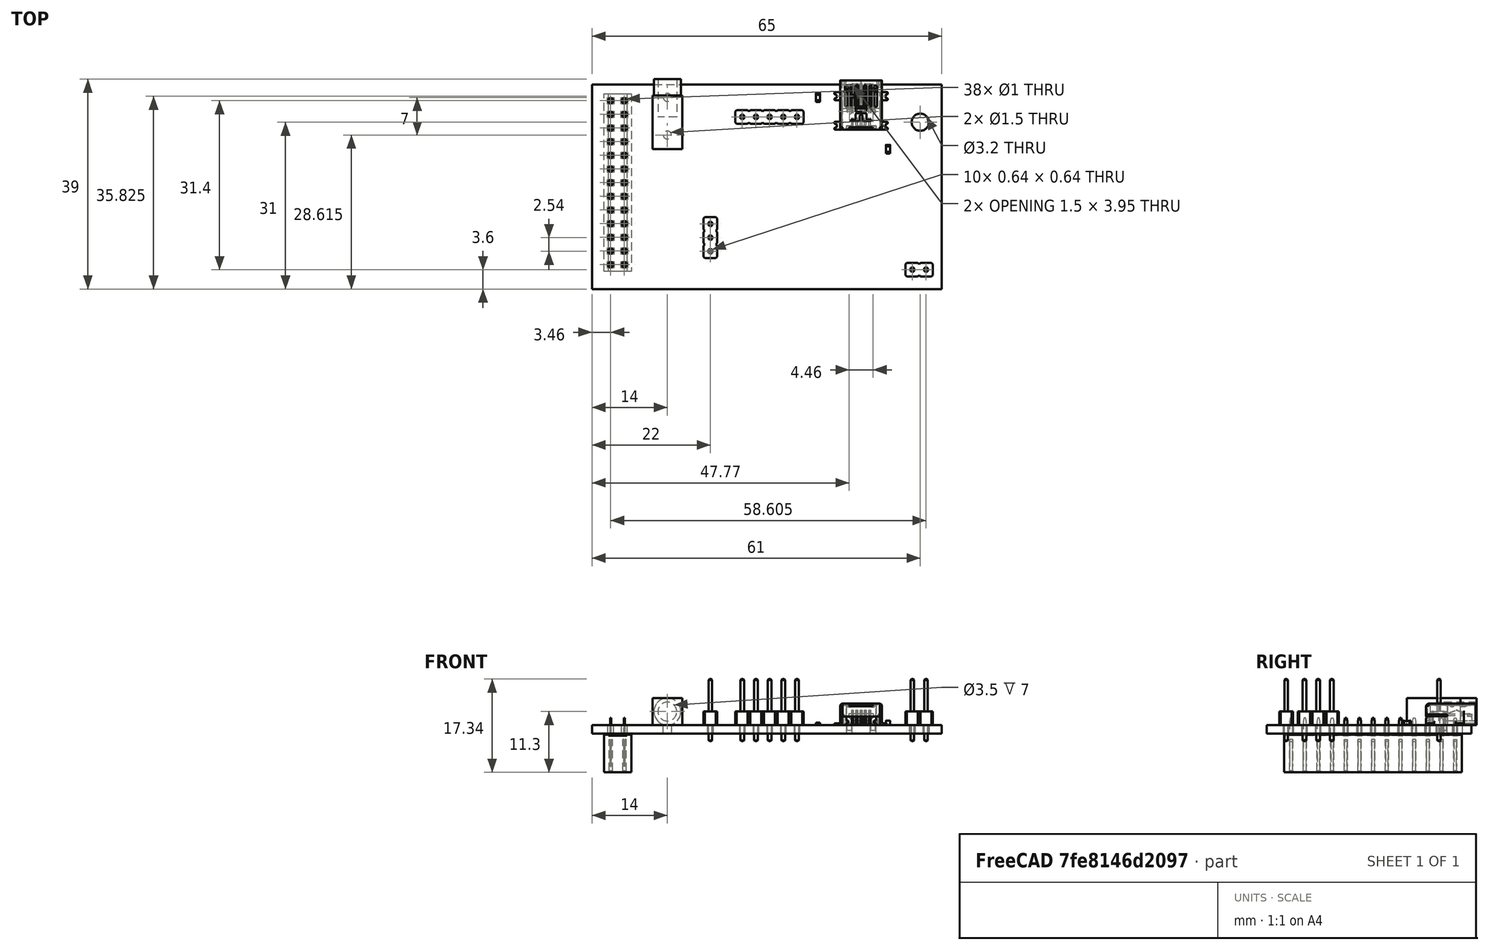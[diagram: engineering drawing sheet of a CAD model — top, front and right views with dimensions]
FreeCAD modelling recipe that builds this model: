
FCSTD DOCUMENT  (FreeCAD 0.20R29177 (Git))
Label: X2GS
License: All rights reserved
LicenseURL: http://en.wikipedia.org/wiki/All_rights_reserved
objects: Part::Feature×8, App::Part×4, PartDesign::CoordinateSystem×1, Sketcher::SketchObject×1, PartDesign::AdditiveBox×1, PartDesign::AdditiveCylinder×1, PartDesign::SubtractiveCylinder×1, PartDesign::Body×1
note: 17 computed .brp shape members not serialized (recipe doc carries the construction recipe); baked Part::Feature solids carry a one-line shape summary decoded from their .brp

FEATURE [PartDesign::CoordinateSystem] Local_CS_a5f0
  AttacherType = Attacher::AttachEngine3D
FEATURE [Part::Feature] Pcb_a5f0
  Placement = pos=(-18,55,0) rot=(0,0,1;0rad)
  shape: bbox 65 x 38 x 1.63 mm, 47 faces (baked)
FEATURE [Sketcher::SketchObject] PCB_Sketch_a5f0
  FullyConstrained = false
  sketch-geometry (4):
    g0: LineSegment StartX=0 StartY=38 StartZ=0 EndX=65 EndY=38 EndZ=0
    g1: LineSegment StartX=65 StartY=38 StartZ=0 EndX=65 EndY=0 EndZ=0
    g2: LineSegment StartX=65 StartY=0 StartZ=0 EndX=0 EndY=0 EndZ=0
    g3: LineSegment StartX=0 StartY=0 StartZ=0 EndX=0 EndY=38 EndZ=0
  constraints (4):
    c: Coincident(g2,g3)
    c: Coincident(g0,g3)
    c: Coincident(g1,g2)
    c: Coincident(g0,g1)
FEATURE [App::Part] Board_Geoms_a5f0
  Group = -> [Local_CS_a5f0,Pcb_a5f0,PCB_Sketch_a5f0]
  Origin = -> Origin
FEATURE [Part::Feature] Shape  label="J2_PinHeader_1x02_P254mm_Vertical_71d739e1dbee"
  Placement = pos=(59.525,3.6,0) rot=(0,0,1;1.5708rad)
  shape: bbox 5.08 x 2.54 x 11.54 mm, 52 faces (baked)
FEATURE [Part::Feature] Shape001  label="J6_PinHeader_1x03_P254mm_Vertical_44f63a92c95c"
  Placement = pos=(22,7,0) rot=(0,0,1;3.14159rad)
  shape: bbox 2.54 x 7.62 x 11.54 mm, 76 faces (baked)
FEATURE [Part::Feature] Shape002  label="J5_USB_Mini-B_Lumberg_2486_01_Horizontal_9461947c8fcd"
  Placement = pos=(50,33,0) rot=(0,0,1;3.14159rad)
  shape: bbox 9.9 x 9.2 x 4.997 mm, 472 faces (baked)
FEATURE [Part::Feature] Shape003  label="C4_C_0603_1608Metric_5884737a9b9c"
  Placement = pos=(55,26,0) rot=(0,0,-1;1.5708rad)
  shape: bbox 0.8 x 1.6 x 0.8 mm, 28 faces (baked)
FEATURE [Part::Feature] Shape004  label="J4_PinHeader_1x05_P254mm_Vertical_864e0cb13e0f"
  Placement = pos=(27.92,32,0) rot=(0,0,1;1.5708rad)
  shape: bbox 12.7 x 2.54 x 11.54 mm, 124 faces (baked)
FEATURE [Part::Feature] Shape005  label="J1_PinSocket_2x13_P254mm_Vertical_392b41559fa7"
  Placement = pos=(3.5,35,-1.8) rot=(0,1,0;3.14159rad)
  shape: bbox 5.08 x 33.02 x 10.1 mm, 816 faces (baked)
FEATURE [Part::Feature] Shape006  label="R1_R_0603_1608Metric_fa31dec0bdac"
  Placement = pos=(42,35.6,0) rot=(0,0,-1;1.5708rad)
  shape: bbox 0.8 x 1.6 x 0.45 mm, 26 faces (baked)
FEATURE [PartDesign::AdditiveBox] Box
  AttacherType = Attacher::AttachEngine3D
  AttachmentOffset = pos=(11.25,26,0) rot=(0,0,1;0rad)
  Height = 5
  Length = 5.5
  MapMode = 5
  Placement = pos=(11.25,26,0) rot=(0,0,1;0rad)
  Support = -> [XY_Plane004]
  Width = 10
FEATURE [PartDesign::AdditiveCylinder] Cylinder
  Angle = 360
  AttacherType = Attacher::AttachEngine3D
  AttachmentOffset = pos=(14,39,2.5) rot=(1,0,0;1.5708rad)
  BaseFeature = -> Box
  FirstAngle = 0
  Height = 3
  MapMode = 5
  Placement = pos=(14,39,2.5) rot=(1,0,0;1.5708rad)
  Radius = 2.5
  SecondAngle = 0
  Support = -> [XY_Plane004]
FEATURE [PartDesign::SubtractiveCylinder] Cylinder001
  Angle = 360
  AttacherType = Attacher::AttachEngine3D
  AttachmentOffset = pos=(14,39,2.5) rot=(1,0,0;1.5708rad)
  BaseFeature = -> Cylinder
  FirstAngle = 0
  Height = 7
  MapMode = 5
  Placement = pos=(14,39,2.5) rot=(1,0,0;1.5708rad)
  Radius = 1.75
  SecondAngle = 0
  Support = -> [XY_Plane004]
FEATURE [PartDesign::Body] Body  label="3.5-jack"
  Group = -> [Box,Cylinder,Cylinder001]
  Origin = -> Origin004
  Tip = -> Cylinder001
FEATURE [App::Part] Top_a5f0
  Group = -> [Shape,Shape001,Shape002,Shape003,Shape004,Shape005,Shape006,Body]
  Origin = -> Origin003
FEATURE [App::Part] Step_Models_a5f0
  Group = -> [Top_a5f0]
  Origin = -> Origin002
FEATURE [App::Part] Board_a5f0  label="X2GS"
  Group = -> [Board_Geoms_a5f0,Step_Models_a5f0]
  Origin = -> Origin001
  Placement = pos=(-32.5,-19,0) rot=(0,0,1;0rad)
